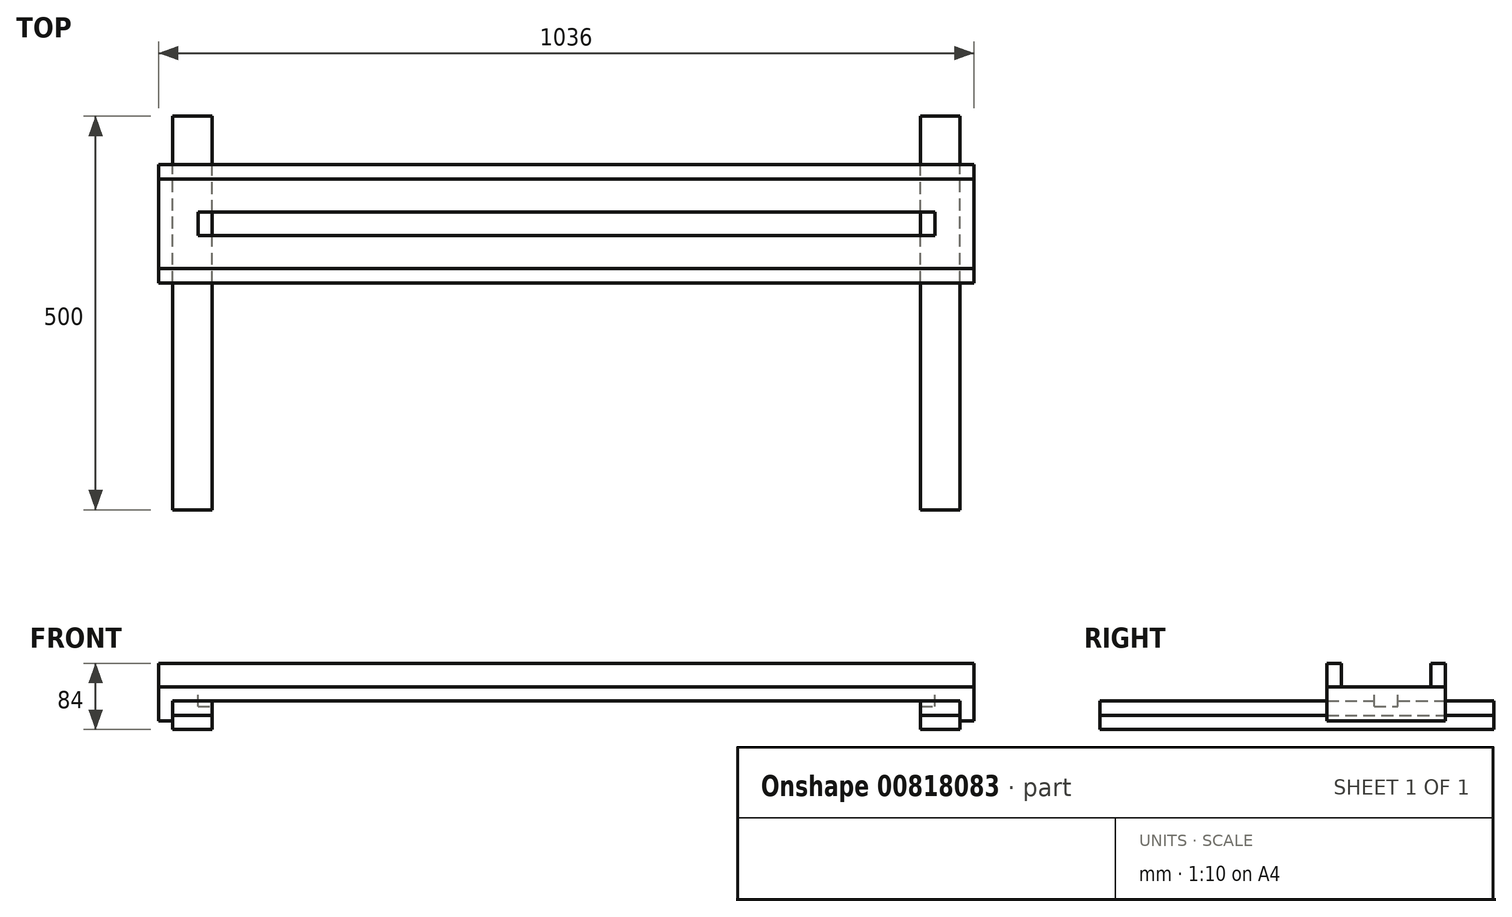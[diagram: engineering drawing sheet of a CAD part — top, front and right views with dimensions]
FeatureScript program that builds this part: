
annotation { "Feature Type Name" : "Feature", "Feature Type Description" : "" }
export const myFeature = defineFeature(function(context is Context, id is Id, definition is map)
    precondition{}
    {
        {
            var Q0;
            Q0=qCreatedBy(makeId("Front.planeOp"),FACE);
            var sketch = newSketch(context, id + "F0", { "sketchPlane" : qUnion([Q0])});
            skLineSegment(sketch, "E0.bottom", {"start": v(-52.39, -8.7) * mm, "end": v(-2.39, -8.7) * mm});
            skLineSegment(sketch, "E0.top", {"start": v(-52.39, -26.7) * mm, "end": v(-2.39, -26.7) * mm});
            skLineSegment(sketch, "E0.left", {"start": v(-52.39, -8.7) * mm, "end": v(-52.39, -26.7) * mm});
            skLineSegment(sketch, "E0.right", {"start": v(-2.39, -8.7) * mm, "end": v(-2.39, -26.7) * mm});
            skSolve(sketch);
        }
        {
            var Q0;
            Q0=makeQuery(id+"F0.imprint","IMPRINT",FACE,{"disambiguationData":[TD([[makeQuery(id+"F0.imprint","IMPRINT",EDGE,{"derivedFrom":sQuery(id+"F0.wireOp",EDGE,"E0.bottom")}),-1.0]])]});
            extrude(context, id + "F1", {"entities" : qUnion([Q0]), "depth" : 500 * mm, "offsetDistance" : 25 * mm});
        }
        {
            var Q0;
            Q0=makeQuery(id+"F1.opExtrude","SWEPT_FACE",FACE,{"disambiguationData":[OSD([sQuery(id+"F0.wireOp",EDGE,"E0.bottom")])]});
            extrude(context, id + "F2", {"entities" : qUnion([Q0]), "depth" : 18 * mm, "offsetDistance" : 25 * mm});
        }
        {
            var Q0;
            Q0=makeQuery(id+"F2.opExtrude","CAP_FACE",FACE,{"disambiguationData":[OSD([sQuery(id+"F0.wireOp",EDGE,"E0.bottom")])],"isStart":false});
            var sketch = newSketch(context, id + "F3", { "sketchPlane" : qUnion([Q0])});
            skLineSegment(sketch, "E1.bottom", {"start": v(-70.39, -61.74) * mm, "end": v(447.61, -61.74) * mm});
            skLineSegment(sketch, "E1.top", {"start": v(-70.39, -211.74) * mm, "end": v(447.61, -211.74) * mm});
            skLineSegment(sketch, "E1.left", {"start": v(-70.39, -61.74) * mm, "end": v(-70.39, -211.74) * mm});
            skLineSegment(sketch, "E1.right", {"start": v(447.61, -61.74) * mm, "end": v(447.61, -211.74) * mm});
            skSolve(sketch);
        }
        {
            var Q0;
            Q0 = qSketchRegion(id + "F3", true);
            extrude(context, id + "F4", {"entities" : qUnion([Q0]), "depth" : 18 * mm, "offsetDistance" : 25 * mm});
        }
        {
            var Q0;
            Q0=makeQuery(id+"F4.opExtrude","CAP_FACE",FACE,{"disambiguationData":[OSD([sQuery(id+"F3.wireOp",EDGE,"E1.bottom"),sQuery(id+"F3.wireOp",EDGE,"E1.top"),sQuery(id+"F3.wireOp",EDGE,"E1.left"),sQuery(id+"F3.wireOp",EDGE,"E1.right")])],"isStart":true});
            var sketch = newSketch(context, id + "F5", { "sketchPlane" : qUnion([Q0])});
            skLineSegment(sketch, "E2.bottom", {"start": v(-70.39, 211.74) * mm, "end": v(-52.39, 211.74) * mm});
            skLineSegment(sketch, "E2.top", {"start": v(-70.39, 61.74) * mm, "end": v(-52.39, 61.74) * mm});
            skLineSegment(sketch, "E2.left", {"start": v(-70.39, 211.74) * mm, "end": v(-70.39, 61.74) * mm});
            skLineSegment(sketch, "E2.right", {"start": v(-52.39, 211.74) * mm, "end": v(-52.39, 61.74) * mm});
            skSolve(sketch);
        }
        {
            var Q0;
            Q0=makeQuery(id+"F5.imprint","IMPRINT",FACE,{"disambiguationData":[TD([[makeQuery(id+"F5.imprint","IMPRINT",EDGE,{"derivedFrom":sQuery(id+"F5.wireOp",EDGE,"E2.bottom")}),-1.0]])]});
            extrude(context, id + "F6", {"entities" : qUnion([Q0]), "depth" : 25 * mm, "offsetDistance" : 25 * mm});
        }
        {
            var Q0;
            Q0=makeQuery(id+"F2.opExtrude","SWEPT_BODY",BODY,{"disambiguationData":[OSD([sQuery(id+"F0.wireOp",EDGE,"E0.bottom")])]});
            var Q1;
            Q1=makeQuery(id+"F1.opExtrude","SWEPT_BODY",BODY,{"disambiguationData":[OSD([sQuery(id+"F0.wireOp",EDGE,"E0.bottom"),sQuery(id+"F0.wireOp",EDGE,"E0.top"),sQuery(id+"F0.wireOp",EDGE,"E0.left"),sQuery(id+"F0.wireOp",EDGE,"E0.right")])]});
            var Q2;
            Q2=makeQuery(id+"F6.opExtrude","SWEPT_BODY",BODY,{"disambiguationData":[OSD([sQuery(id+"F5.wireOp",EDGE,"E2.bottom"),sQuery(id+"F5.wireOp",EDGE,"E2.top"),sQuery(id+"F5.wireOp",EDGE,"E2.left"),sQuery(id+"F5.wireOp",EDGE,"E2.right")])]});
            var Q3;
            Q3=makeQuery(id+"F4.opExtrude","SWEPT_FACE",FACE,{"disambiguationData":[OSD([sQuery(id+"F3.wireOp",EDGE,"E1.right")])]});
            mirror(context, id + "F7", {"entities" : qUnion([Q0, Q1, Q2]), "mirrorPlane" : qUnion([Q3])});
        }
        {
            var Q0;
            Q0=makeQuery(id+"F4.opExtrude","SWEPT_BODY",BODY,{"disambiguationData":[OSD([sQuery(id+"F3.wireOp",EDGE,"E1.bottom"),sQuery(id+"F3.wireOp",EDGE,"E1.top"),sQuery(id+"F3.wireOp",EDGE,"E1.left"),sQuery(id+"F3.wireOp",EDGE,"E1.right")])]});
            var Q1;
            Q1=makeQuery(id+"F4.opExtrude","SWEPT_FACE",FACE,{"disambiguationData":[OSD([sQuery(id+"F3.wireOp",EDGE,"E1.right")])]});
            mirror(context, id + "F8", {"operationType" : NewBodyOperationType.ADD, "entities" : qUnion([Q0]), "mirrorPlane" : qUnion([Q1])});
        }
        {
            var Q0;
            {var subQ0=makeQuery(id+"F4.opExtrude","CAP_FACE",FACE,{"disambiguationData":[OSD([sQuery(id+"F3.wireOp",EDGE,"E1.bottom"),sQuery(id+"F3.wireOp",EDGE,"E1.top"),sQuery(id+"F3.wireOp",EDGE,"E1.left"),sQuery(id+"F3.wireOp",EDGE,"E1.right")])],"isStart":false});Q0=makeQuery(id+"F8.boolean.opBoolean","MERGE",FACE,{"derivedFrom":[subQ0,makeQuery(id+"F8.opPattern","COPY",FACE,{"derivedFrom":subQ0,"instanceName":"1"})]});}
            var sketch = newSketch(context, id + "F9", { "sketchPlane" : qUnion([Q0])});
            skLineSegment(sketch, "E3.bottom", {"start": v(-70.39, -61.74) * mm, "end": v(965.61, -61.74) * mm});
            skLineSegment(sketch, "E3.top", {"start": v(-70.39, -79.74) * mm, "end": v(965.61, -79.74) * mm});
            skLineSegment(sketch, "E3.left", {"start": v(-70.39, -61.74) * mm, "end": v(-70.39, -79.74) * mm});
            skLineSegment(sketch, "E3.right", {"start": v(965.61, -61.74) * mm, "end": v(965.61, -79.74) * mm});
            skLineSegment(sketch, "E4.bottom", {"start": v(965.61, -211.74) * mm, "end": v(-70.39, -211.74) * mm});
            skLineSegment(sketch, "E4.top", {"start": v(965.61, -193.74) * mm, "end": v(-70.39, -193.74) * mm});
            skLineSegment(sketch, "E4.left", {"start": v(965.61, -211.74) * mm, "end": v(965.61, -193.74) * mm});
            skLineSegment(sketch, "E4.right", {"start": v(-70.39, -211.74) * mm, "end": v(-70.39, -193.74) * mm});
            skLineSegment(sketch, "E5.bottom", {"start": v(-20.39, -121.74) * mm, "end": v(915.61, -121.74) * mm});
            skLineSegment(sketch, "E5.top", {"start": v(-20.39, -151.74) * mm, "end": v(915.61, -151.74) * mm});
            skLineSegment(sketch, "E5.left", {"start": v(-20.39, -121.74) * mm, "end": v(-20.39, -151.74) * mm});
            skLineSegment(sketch, "E5.right", {"start": v(915.61, -121.74) * mm, "end": v(915.61, -151.74) * mm});
            skSolve(sketch);
        }
        {
            var Q0;
            Q0=makeQuery(id+"F9.imprint","IMPRINT",FACE,{"disambiguationData":[TD([[makeQuery(id+"F9.imprint","IMPRINT",EDGE,{"derivedFrom":sQuery(id+"F9.wireOp",EDGE,"E3.bottom")}),-1.0]])]});
            var Q1;
            Q1=makeQuery(id+"F9.imprint","IMPRINT",FACE,{"disambiguationData":[TD([[makeQuery(id+"F9.imprint","IMPRINT",EDGE,{"derivedFrom":sQuery(id+"F9.wireOp",EDGE,"E4.bottom")}),1.0]])]});
            extrude(context, id + "F10", {"entities" : qUnion([Q0, Q1]), "depth" : 30 * mm, "offsetDistance" : 25 * mm});
        }
        {
            var Q0;
            Q0=makeQuery(id+"F9.imprint","IMPRINT",FACE,{"disambiguationData":[TD([[makeQuery(id+"F9.imprint","IMPRINT",EDGE,{"derivedFrom":sQuery(id+"F9.wireOp",EDGE,"E5.bottom")}),-1.0]])]});
            extrude(context, id + "F11", {"entities" : qUnion([Q0]), "operationType" : NewBodyOperationType.REMOVE, "oppositeDirection" : true, "depth" : 25 * mm, "offsetDistance" : 25 * mm});
        }
    });
